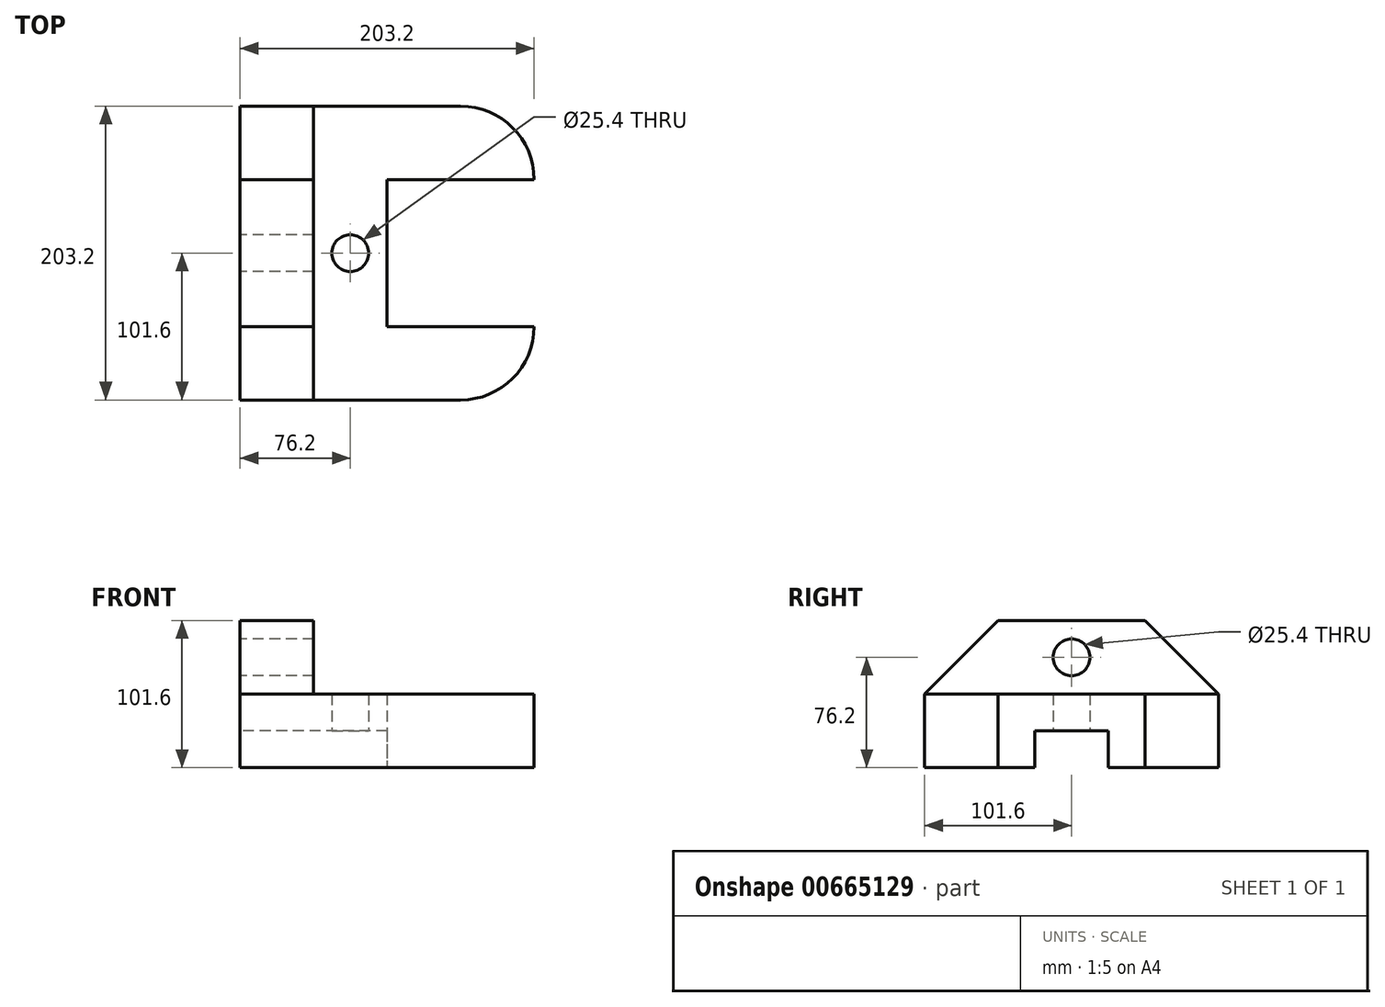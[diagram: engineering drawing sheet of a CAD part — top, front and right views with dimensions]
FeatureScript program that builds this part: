
annotation { "Feature Type Name" : "Feature", "Feature Type Description" : "" }
export const myFeature = defineFeature(function(context is Context, id is Id, definition is map)
    precondition{}
    {
        {
            var Q0;
            Q0=qCreatedBy(makeId("Top.planeOp"),FACE);
            var sketch = newSketch(context, id + "F0", { "sketchPlane" : qUnion([Q0])});
            skLineSegment(sketch, "E0", {"start": v(0, 0) * mm, "end": v(0, -203.2) * mm});
            skLineSegment(sketch, "E1", {"start": v(0, -203.2) * mm, "end": v(50.8, -203.2) * mm});
            skLineSegment(sketch, "E2", {"start": v(50.8, -203.2) * mm, "end": v(50.8, -152.4) * mm});
            skLineSegment(sketch, "E3", {"start": v(50.8, -152.4) * mm, "end": v(0, -152.4) * mm});
            skLineSegment(sketch, "E4", {"start": v(50.8, -203.2) * mm, "end": v(152.4, -203.2) * mm});
            skLineSegment(sketch, "E5", {"start": v(152.4, -203.2) * mm, "end": v(152.4, -152.4) * mm});
            skLineSegment(sketch, "E6", {"start": v(152.4, -152.4) * mm, "end": v(101.6, -152.4) * mm});
            skLineSegment(sketch, "E7", {"start": v(101.6, -152.4) * mm, "end": v(101.6, -50.8) * mm});
            skLineSegment(sketch, "E8", {"start": v(101.6, -50.8) * mm, "end": v(152.4, -50.8) * mm});
            skLineSegment(sketch, "E9", {"start": v(152.4, -50.8) * mm, "end": v(152.4, 0) * mm});
            skLineSegment(sketch, "E10", {"start": v(152.4, 0) * mm, "end": v(50.8, 0) * mm});
            skLineSegment(sketch, "E11", {"start": v(50.8, 0) * mm, "end": v(0, 0) * mm});
            skLineSegment(sketch, "E12", {"start": v(50.8, 0) * mm, "end": v(50.8, -50.8) * mm});
            skLineSegment(sketch, "E13", {"start": v(50.8, -50.8) * mm, "end": v(0, -50.8) * mm});
            skLineSegment(sketch, "E14", {"start": v(152.4, -152.4) * mm, "end": v(203.2, -152.4) * mm});
            skLineSegment(sketch, "E15", {"start": v(152.4, -50.8) * mm, "end": v(203.2, -50.8) * mm});
            skArc(sketch, "E16", {"start": v(203.2, -50.8) * mm, "mid": v(188.32, -14.88) * mm, "end": v(152.4, 0) * mm});
            skArc(sketch, "E17", {"start": v(152.4, -203.2) * mm, "mid": v(188.32, -188.32) * mm, "end": v(203.2, -152.4) * mm});
            skLineSegment(sketch, "E18", {"start": v(50.8, -50.8) * mm, "end": v(50.8, -152.4) * mm});
            skCircle(sketch, "E19", {"center": v(76.2, -101.6) * mm, "radius": 12.7 * mm});
            skSolve(sketch);
        }
        {
            var Q0;
            {var subQ0=sQuery(id+"F0.wireOp",EDGE,"E11");Q0=makeQuery(id+"F0.imprint","IMPRINT",FACE,{"disambiguationData":[TD([[makeQuery(id+"F0.imprint","IMPRINT",EDGE,{"derivedFrom":subQ0}),1.0]])]});}
            var Q1;
            {var subQ0=sQuery(id+"F0.wireOp",EDGE,"E3");Q1=makeQuery(id+"F0.imprint","IMPRINT",FACE,{"disambiguationData":[TD([[makeQuery(id+"F0.imprint","IMPRINT",EDGE,{"derivedFrom":subQ0}),-1.0]])]});}
            var Q2;
            {var subQ0=sQuery(id+"F0.wireOp",EDGE,"E1");Q2=makeQuery(id+"F0.imprint","IMPRINT",FACE,{"disambiguationData":[TD([[makeQuery(id+"F0.imprint","IMPRINT",EDGE,{"derivedFrom":subQ0}),1.0]])]});}
            extrude(context, id + "F1", {"entities" : qUnion([Q0, Q1, Q2]), "depth" : 101.6 * mm, "offsetDistance" : 25.4 * mm});
        }
        {
            var Q0;
            Q0=makeQuery(id+"F0.imprint","IMPRINT",FACE,{"disambiguationData":[TD([[makeQuery(id+"F0.imprint","IMPRINT",EDGE,{"derivedFrom":sQuery(id+"F0.wireOp",EDGE,"E9")}),-1.0]])]});
            var Q1;
            Q1=makeQuery(id+"F0.imprint","IMPRINT",FACE,{"disambiguationData":[TD([[makeQuery(id+"F0.imprint","IMPRINT",EDGE,{"derivedFrom":sQuery(id+"F0.wireOp",EDGE,"E2")}),-1.0]])]});
            var Q2;
            Q2=makeQuery(id+"F0.imprint","IMPRINT",FACE,{"disambiguationData":[TD([[makeQuery(id+"F0.imprint","IMPRINT",EDGE,{"derivedFrom":sQuery(id+"F0.wireOp",EDGE,"E5")}),-1.0]])]});
            extrude(context, id + "F2", {"entities" : qUnion([Q0, Q1, Q2]), "operationType" : NewBodyOperationType.ADD, "depth" : 50.8 * mm, "offsetDistance" : 25.4 * mm});
        }
        {
            var Q0;
            Q0=qCreatedBy(makeId("Right.planeOp"),FACE);
            var sketch = newSketch(context, id + "F3", { "sketchPlane" : qUnion([Q0])});
            skLineSegment(sketch, "E20", {"start": v(0, 0) * mm, "end": v(-76.2, 0) * mm});
            skLineSegment(sketch, "E21", {"start": v(-76.2, 0) * mm, "end": v(-76.2, 25.4) * mm});
            skLineSegment(sketch, "E22", {"start": v(-76.2, 25.4) * mm, "end": v(-127, 25.4) * mm});
            skLineSegment(sketch, "E23", {"start": v(-127, 25.4) * mm, "end": v(-127, 0) * mm});
            skLineSegment(sketch, "E24", {"start": v(-127, 0) * mm, "end": v(-76.2, 0) * mm});
            skLineSegment(sketch, "E25", {"start": v(-101.6, 25.4) * mm, "end": v(-101.6, 76.2) * mm});
            skCircle(sketch, "E26", {"center": v(-101.6, 76.2) * mm, "radius": 12.7 * mm});
            skSolve(sketch);
        }
        {
            var Q0;
            Q0 = qSketchRegion(id + "F3", true);
            extrude(context, id + "F4", {"entities" : qUnion([Q0]), "operationType" : NewBodyOperationType.REMOVE, "endBound" : BoundingType.THROUGH_ALL, "depth" : 25.4 * mm, "offsetDistance" : 25.4 * mm});
        }
        {
            var Q0;
            Q0=makeQuery(id+"F1.opExtrude","CAP_EDGE",EDGE,{"disambiguationData":[OSD([sQuery(id+"F0.wireOp",EDGE,"E1")])],"isStart":false});
            var Q1;
            Q1=makeQuery(id+"F1.opExtrude","CAP_EDGE",EDGE,{"disambiguationData":[OSD([sQuery(id+"F0.wireOp",EDGE,"E11")])],"isStart":false});
            chamfer(context, id + "F5", {"entities" : qUnion([Q0, Q1]), "width" : 50.8 * mm, "tangentPropagation" : true});
        }
    });
